annotation { "Feature Type Name" : "Feature", "Feature Type Description" : "" }
export const myFeature = defineFeature(function(context is Context, id is Id, definition is map)
    precondition{}
    {
        {
            var Q0;
            Q0=qCreatedBy(makeId("Top.planeOp"),FACE);
            var sketch = newSketch(context, id + "F0", { "sketchPlane" : qUnion([Q0])});
            skLineSegment(sketch, "E0", {"start": v(0, -673.1) * mm, "end": v(0, 901.7) * mm});
            skLineSegment(sketch, "E1", {"start": v(0, 901.7) * mm, "end": v(438.15, 901.7) * mm});
            skLineSegment(sketch, "E2", {"start": v(438.15, 901.7) * mm, "end": v(438.15, 0) * mm});
            skLineSegment(sketch, "E3", {"start": v(438.15, 0) * mm, "end": v(1454.15, 0) * mm});
            skLineSegment(sketch, "E4.0", {"start": v(552.45, 114.3) * mm, "end": v(1454.15, 114.3) * mm});
            skLineSegment(sketch, "E4.1", {"start": v(552.45, 1016) * mm, "end": v(552.45, 114.3) * mm});
            skLineSegment(sketch, "E4.2", {"start": v(-114.3, 1016) * mm, "end": v(552.45, 1016) * mm});
            skLineSegment(sketch, "E4.3", {"start": v(-114.3, -673.1) * mm, "end": v(-114.3, 1016) * mm});
            skLineSegment(sketch, "E5.0", {"start": v(425.45, -12.7) * mm, "end": v(1454.15, -12.7) * mm});
            skLineSegment(sketch, "E5.1", {"start": v(425.45, 889) * mm, "end": v(425.45, -12.7) * mm});
            skLineSegment(sketch, "E5.2", {"start": v(12.7, 889) * mm, "end": v(425.45, 889) * mm});
            skLineSegment(sketch, "E5.3", {"start": v(12.7, -673.1) * mm, "end": v(12.7, 889) * mm});
            skFitSpline(sketch, "E6", {"points": [v(-114.3, -673.1) * mm, v(0, -673.1) * mm, v(12.7, -673.1) * mm], "startDerivative": vector(215.33, 101.54) * mm, "endDerivative": vector(15.02, 74.43) * mm});
            skFitSpline(sketch, "E7", {"points": [v(1454.15, 114.3) * mm, v(1454.15, 0) * mm, v(1454.15, -12.7) * mm], "startDerivative": vector(-157.16, -195.04) * mm, "endDerivative": vector(-135.93, -152.4) * mm});
            skLineSegment(sketch, "E8.bottom", {"start": v(30.7, -669.3) * mm, "end": v(1447.96, -669.3) * mm, "construction": true});
            skLineSegment(sketch, "E8.top", {"start": v(30.7, -660.4) * mm, "end": v(1447.96, -660.4) * mm, "construction": true});
            skLineSegment(sketch, "E8.left", {"start": v(30.7, -669.3) * mm, "end": v(30.7, -660.4) * mm, "construction": true});
            skLineSegment(sketch, "E8.right", {"start": v(1447.96, -669.3) * mm, "end": v(1447.96, -660.4) * mm, "construction": true});
            skLineSegment(sketch, "E9", {"start": v(27.37, -457.2) * mm, "end": v(1426.84, -457.2) * mm, "construction": true});
            skText(sketch, "E10", { "text": "Clothes\n", "fontName": "OpenSans-Regular.ttf"});
            skText(sketch, "E11", { "text": "Hanger Rod", "fontName": "OpenSans-Regular.ttf"});
            skLineSegment(sketch, "E12", {"start": v(-114.3, 584.2) * mm, "end": v(0, 584.2) * mm, "construction": true});
            skLineSegment(sketch, "E13", {"start": v(-114.3, 177.8) * mm, "end": v(0, 177.8) * mm, "construction": true});
            skLineSegment(sketch, "E14", {"start": v(438.15, 556.05) * mm, "end": v(552.45, 556.05) * mm, "construction": true});
            skLineSegment(sketch, "E15", {"start": v(958.85, 0) * mm, "end": v(958.85, 114.3) * mm, "construction": true});
            const initialGuessF0  = {"E10": [1.1723, -0.49137, 1, 0, 0.01667], "E11": [1.16785, -0.64477, 1, 0, 0.02]};
            skSetInitialGuess(sketch, initialGuessF0);
            skSolve(sketch);
        }
        {
            var Q0;
            {var subQ2=sQuery(id+"F0.wireOp",EDGE,"E0");Q0=makeQuery(id+"F0.imprint","IMPRINT",FACE,{"disambiguationData":[TD([[makeQuery(id+"F0.imprint","IMPRINT",EDGE,{"derivedFrom":subQ2}),-1.0]])]});}
            var Q1;
            Q1=sQuery(id+"F0.wireOp",EDGE,"E0");
            var Q2;
            Q2=sQuery(id+"F0.wireOp",EDGE,"E1");
            var Q3;
            Q3=sQuery(id+"F0.wireOp",EDGE,"E2");
            var Q4;
            Q4=sQuery(id+"F0.wireOp",EDGE,"E5.1");
            var Q5;
            Q5=sQuery(id+"F0.wireOp",EDGE,"E5.2");
            var Q6;
            Q6=sQuery(id+"F0.wireOp",EDGE,"E5.3");
            var Q7;
            Q7=sQuery(id+"F0.wireOp",EDGE,"E3");
            var Q8;
            Q8=sQuery(id+"F0.wireOp",EDGE,"E5.0");
            extrude(context, id + "F1", {"entities" : qUnion([Q0]), "surfaceEntities" : qUnion([Q1, Q2, Q3, Q4, Q5, Q6, Q7, Q8]), "depth" : 127 * mm, "offsetDistance" : 25.4 * mm});
        }
        {
            var Q0;
            Q0=qCreatedBy(makeId("Front.planeOp"),FACE);
            var sketch = newSketch(context, id + "F2", { "sketchPlane" : qUnion([Q0])});
            skLineSegment(sketch, "E16.bottom", {"start": v(0, 0) * mm, "end": v(12.7, 0) * mm, "construction": true});
            skLineSegment(sketch, "E16.top", {"start": v(0, 127) * mm, "end": v(12.7, 127) * mm, "construction": true});
            skLineSegment(sketch, "E16.left", {"start": v(0, 0) * mm, "end": v(0, 127) * mm, "construction": true});
            skLineSegment(sketch, "E16.right", {"start": v(12.7, 0) * mm, "end": v(12.7, 127) * mm, "construction": true});
            skLineSegment(sketch, "E17.bottom", {"start": v(438.15, 0) * mm, "end": v(425.45, 0) * mm, "construction": true});
            skLineSegment(sketch, "E17.top", {"start": v(438.15, 127) * mm, "end": v(425.45, 127) * mm, "construction": true});
            skLineSegment(sketch, "E17.left", {"start": v(438.15, 0) * mm, "end": v(438.15, 127) * mm, "construction": true});
            skLineSegment(sketch, "E17.right", {"start": v(425.45, 0) * mm, "end": v(425.45, 127) * mm, "construction": true});
            skLineSegment(sketch, "E18.bottom", {"start": v(0, 0) * mm, "end": v(438.15, 0) * mm, "construction": true});
            skLineSegment(sketch, "E18.top", {"start": v(0, 2438.4) * mm, "end": v(438.15, 2438.4) * mm, "construction": true});
            skLineSegment(sketch, "E18.left", {"start": v(0, 0) * mm, "end": v(0, 2438.4) * mm, "construction": true});
            skLineSegment(sketch, "E18.right", {"start": v(438.15, 0) * mm, "end": v(438.15, 2438.4) * mm, "construction": true});
            skLineSegment(sketch, "E19", {"start": v(958.85, 0) * mm, "end": v(958.85, 2438.4) * mm, "construction": true});
            skLineSegment(sketch, "E20", {"start": v(565.15, 0) * mm, "end": v(565.15, 2438.4) * mm, "construction": true});
            skSolve(sketch);
        }
        {
            var Q0;
            Q0=qCreatedBy(makeId("Front.planeOp"),FACE);
            cPlane(context, id + "F3", {"entities" : qUnion([Q0]), "cplaneType" : CPlaneType.OFFSET, "offset" : 17.45 * mm, "width" : 152.4 * mm, "height" : 152.4 * mm});
        }
        {
            var Q0;
            Q0=qCreatedBy(id+"F3.planeOp",FACE);
            var sketch = newSketch(context, id + "F4", { "sketchPlane" : qUnion([Q0])});
            skLineSegment(sketch, "E21.bottom", {"start": v(55.58, 139.7) * mm, "end": v(569.93, 139.7) * mm});
            skLineSegment(sketch, "E21.top", {"start": v(55.58, 1676.4) * mm, "end": v(569.93, 1676.4) * mm});
            skLineSegment(sketch, "E21.left", {"start": v(55.58, 139.7) * mm, "end": v(55.58, 1676.4) * mm});
            skLineSegment(sketch, "E21.right", {"start": v(569.93, 139.7) * mm, "end": v(569.93, 1676.4) * mm});
            skLineSegment(sketch, "E22", {"start": v(55.58, 1295.4) * mm, "end": v(569.93, 1295.4) * mm});
            skLineSegment(sketch, "E23", {"start": v(55.58, 914.4) * mm, "end": v(569.93, 914.4) * mm});
            skLineSegment(sketch, "E24", {"start": v(55.58, 533.4) * mm, "end": v(569.93, 533.4) * mm});
            skLineSegment(sketch, "E25", {"start": v(55.58, 152.4) * mm, "end": v(569.93, 152.4) * mm, "construction": true});
            skCircle(sketch, "E26", {"center": v(109.55, 1631.95) * mm, "radius": 4.33 * mm});
            skCircle(sketch, "E27", {"center": v(109.55, 1339.85) * mm, "radius": 4.33 * mm});
            skCircle(sketch, "E28", {"center": v(109.55, 1250.95) * mm, "radius": 4.33 * mm});
            skCircle(sketch, "E29", {"center": v(109.55, 958.85) * mm, "radius": 4.33 * mm});
            skCircle(sketch, "E30", {"center": v(109.55, 869.95) * mm, "radius": 4.33 * mm});
            skCircle(sketch, "E31", {"center": v(109.55, 577.85) * mm, "radius": 4.33 * mm});
            skCircle(sketch, "E32", {"center": v(109.55, 488.95) * mm, "radius": 4.33 * mm});
            skCircle(sketch, "E33", {"center": v(109.55, 196.85) * mm, "radius": 4.33 * mm});
            skLineSegment(sketch, "E34", {"start": v(109.55, 1631.95) * mm, "end": v(109.55, 196.85) * mm, "construction": true});
            skCircle(sketch, "E35", {"center": v(515.95, 1631.95) * mm, "radius": 4.33 * mm});
            skCircle(sketch, "E36", {"center": v(515.95, 1339.85) * mm, "radius": 4.33 * mm});
            skCircle(sketch, "E37", {"center": v(515.95, 1250.95) * mm, "radius": 4.33 * mm});
            skCircle(sketch, "E38", {"center": v(515.95, 958.85) * mm, "radius": 4.33 * mm});
            skCircle(sketch, "E39", {"center": v(515.95, 869.95) * mm, "radius": 4.33 * mm});
            skCircle(sketch, "E40", {"center": v(515.95, 577.85) * mm, "radius": 4.33 * mm});
            skCircle(sketch, "E41", {"center": v(515.95, 488.95) * mm, "radius": 4.33 * mm});
            skCircle(sketch, "E42", {"center": v(515.95, 196.85) * mm, "radius": 4.33 * mm});
            skLineSegment(sketch, "E43", {"start": v(515.95, 1631.95) * mm, "end": v(515.95, 196.85) * mm, "construction": true});
            skLineSegment(sketch, "E44", {"start": v(109.55, 1631.95) * mm, "end": v(515.95, 1631.95) * mm, "construction": true});
            skLineSegment(sketch, "E45", {"start": v(109.55, 196.85) * mm, "end": v(515.95, 196.85) * mm, "construction": true});
            skLineSegment(sketch, "E46", {"start": v(109.55, 488.95) * mm, "end": v(515.95, 488.95) * mm, "construction": true});
            skLineSegment(sketch, "E47", {"start": v(109.55, 577.85) * mm, "end": v(515.95, 577.85) * mm, "construction": true});
            skLineSegment(sketch, "E48", {"start": v(109.55, 869.95) * mm, "end": v(515.95, 869.95) * mm, "construction": true});
            skLineSegment(sketch, "E49", {"start": v(109.55, 958.85) * mm, "end": v(515.95, 958.85) * mm, "construction": true});
            skLineSegment(sketch, "E50", {"start": v(109.55, 1250.95) * mm, "end": v(515.95, 1250.95) * mm, "construction": true});
            skLineSegment(sketch, "E51", {"start": v(109.55, 1339.85) * mm, "end": v(515.95, 1339.85) * mm, "construction": true});
            skSolve(sketch);
        }
        {
            var Q0;
            Q0=qCreatedBy(makeId("Front.planeOp"),FACE);
            var Q1;
            Q1=qBodyType(qCreatedBy(id+"F14",EDGE),BodyType.WIRE);
            cPlane(context, id + "F5", {"entities" : qUnion([Q0, Q1]), "cplaneType" : CPlaneType.OFFSET, "offset" : 12.7 * mm, "width" : 152.4 * mm, "height" : 152.4 * mm});
        }
        {
            var Q0;
            Q0=qCreatedBy(id+"F5.planeOp",FACE);
            var sketch = newSketch(context, id + "F6", { "sketchPlane" : qUnion([Q0])});
            skLineSegment(sketch, "E52", {"start": v(3.17, 177.8) * mm, "end": v(3.18, 130.18) * mm});
            skLineSegment(sketch, "E53", {"start": v(3.18, 130.18) * mm, "end": v(15.87, 130.18) * mm});
            skLineSegment(sketch, "E54", {"start": v(15.87, 130.18) * mm, "end": v(15.88, 0) * mm});
            skLineSegment(sketch, "E55", {"start": v(15.87, 0) * mm, "end": v(1219.2, 0) * mm});
            skLineSegment(sketch, "E56", {"start": v(1219.2, 0) * mm, "end": v(1219.2, 2438.4) * mm});
            skLineSegment(sketch, "E57", {"start": v(1219.2, 2438.4) * mm, "end": v(0, 2438.4) * mm});
            skLineSegment(sketch, "E58", {"start": v(0, 2438.4) * mm, "end": v(0, 1651) * mm});
            skLineSegment(sketch, "E59", {"start": v(0, 1651) * mm, "end": v(544.53, 1651) * mm});
            skLineSegment(sketch, "E60", {"start": v(544.53, 1651) * mm, "end": v(544.53, 177.8) * mm});
            skLineSegment(sketch, "E61", {"start": v(544.53, 177.8) * mm, "end": v(3.17, 177.8) * mm});
            skSolve(sketch);
        }
        {
            var Q0;
            Q0=makeQuery(id+"F6.imprint","IMPRINT",FACE,{"disambiguationData":[TD([[makeQuery(id+"F6.imprint","IMPRINT",EDGE,{"derivedFrom":sQuery(id+"F6.wireOp",EDGE,"E52")}),1.0]])]});
            extrude(context, id + "F7", {"entities" : qUnion([Q0]), "depth" : 4.75 * mm, "offsetDistance" : 25.4 * mm});
        }
        {
            var Q0;
            Q0=qCreatedBy(id+"F5.planeOp",FACE);
            var sketch = newSketch(context, id + "F8", { "sketchPlane" : qUnion([Q0])});
            skLineSegment(sketch, "E62.bottom", {"start": v(1219.2, 2438.4) * mm, "end": v(1181.1, 2438.4) * mm});
            skLineSegment(sketch, "E62.top", {"start": v(1219.2, 133.35) * mm, "end": v(1181.1, 133.35) * mm});
            skLineSegment(sketch, "E62.left", {"start": v(1219.2, 2438.4) * mm, "end": v(1219.2, 133.35) * mm});
            skLineSegment(sketch, "E62.right", {"start": v(1181.1, 2438.4) * mm, "end": v(1181.1, 133.35) * mm});
            skLineSegment(sketch, "E63.bottom", {"start": v(38.1, 1689.1) * mm, "end": v(1181.1, 1689.1) * mm});
            skLineSegment(sketch, "E63.top", {"start": v(38.1, 1651) * mm, "end": v(1181.1, 1651) * mm});
            skLineSegment(sketch, "E63.right", {"start": v(1181.1, 1689.1) * mm, "end": v(1181.1, 1651) * mm});
            skLineSegment(sketch, "E64.bottom", {"start": v(38.1, 1936.75) * mm, "end": v(1181.1, 1936.75) * mm});
            skLineSegment(sketch, "E64.top", {"start": v(38.1, 1898.65) * mm, "end": v(1181.1, 1898.65) * mm});
            skLineSegment(sketch, "E64.left", {"start": v(38.1, 1936.75) * mm, "end": v(38.1, 1898.65) * mm});
            skLineSegment(sketch, "E64.right", {"start": v(1181.1, 1936.75) * mm, "end": v(1181.1, 1898.65) * mm});
            skLineSegment(sketch, "E65.bottom", {"start": v(38.1, 2190.75) * mm, "end": v(1181.1, 2190.75) * mm});
            skLineSegment(sketch, "E65.top", {"start": v(38.1, 2152.65) * mm, "end": v(1181.1, 2152.65) * mm});
            skLineSegment(sketch, "E65.left", {"start": v(38.1, 2190.75) * mm, "end": v(38.1, 2152.65) * mm});
            skLineSegment(sketch, "E65.right", {"start": v(1181.1, 2190.75) * mm, "end": v(1181.1, 2152.65) * mm});
            skLineSegment(sketch, "E66.bottom", {"start": v(38.1, 2438.4) * mm, "end": v(1181.1, 2438.4) * mm});
            skLineSegment(sketch, "E66.top", {"start": v(38.1, 2400.3) * mm, "end": v(1181.1, 2400.3) * mm});
            skLineSegment(sketch, "E66.left", {"start": v(38.1, 2438.4) * mm, "end": v(38.1, 2400.3) * mm});
            skLineSegment(sketch, "E66.right", {"start": v(1181.1, 2438.4) * mm, "end": v(1181.1, 2400.3) * mm});
            skLineSegment(sketch, "E67.bottom", {"start": v(582.63, 1377.95) * mm, "end": v(1181.1, 1377.95) * mm});
            skLineSegment(sketch, "E67.top", {"start": v(582.63, 1339.85) * mm, "end": v(1181.1, 1339.85) * mm});
            skLineSegment(sketch, "E67.left", {"start": v(582.63, 1377.95) * mm, "end": v(582.63, 1339.85) * mm});
            skLineSegment(sketch, "E67.right", {"start": v(1181.1, 1377.95) * mm, "end": v(1181.1, 1339.85) * mm});
            skLineSegment(sketch, "E68.bottom", {"start": v(544.53, 1651) * mm, "end": v(582.63, 1651) * mm});
            skLineSegment(sketch, "E68.top", {"start": v(544.53, 133.35) * mm, "end": v(582.63, 133.35) * mm});
            skLineSegment(sketch, "E68.left", {"start": v(544.53, 1651) * mm, "end": v(544.53, 133.35) * mm});
            skLineSegment(sketch, "E68.right", {"start": v(582.63, 1651) * mm, "end": v(582.63, 133.35) * mm});
            skLineSegment(sketch, "E69.bottom", {"start": v(582.63, 1073.15) * mm, "end": v(1181.1, 1073.15) * mm});
            skLineSegment(sketch, "E69.top", {"start": v(582.63, 1035.05) * mm, "end": v(1181.1, 1035.05) * mm});
            skLineSegment(sketch, "E69.left", {"start": v(582.63, 1073.15) * mm, "end": v(582.63, 1035.05) * mm});
            skLineSegment(sketch, "E69.right", {"start": v(1181.1, 1073.15) * mm, "end": v(1181.1, 1035.05) * mm});
            skLineSegment(sketch, "E70.bottom", {"start": v(582.63, 768.35) * mm, "end": v(1181.1, 768.35) * mm});
            skLineSegment(sketch, "E70.top", {"start": v(582.63, 730.25) * mm, "end": v(1181.1, 730.25) * mm});
            skLineSegment(sketch, "E70.left", {"start": v(582.63, 768.35) * mm, "end": v(582.63, 730.25) * mm});
            skLineSegment(sketch, "E70.right", {"start": v(1181.1, 768.35) * mm, "end": v(1181.1, 730.25) * mm});
            skLineSegment(sketch, "E71.bottom", {"start": v(582.63, 463.55) * mm, "end": v(1181.1, 463.55) * mm});
            skLineSegment(sketch, "E71.top", {"start": v(582.63, 425.45) * mm, "end": v(1181.1, 425.45) * mm});
            skLineSegment(sketch, "E71.left", {"start": v(582.63, 463.55) * mm, "end": v(582.63, 425.45) * mm});
            skLineSegment(sketch, "E71.right", {"start": v(1181.1, 463.55) * mm, "end": v(1181.1, 425.45) * mm});
            skLineSegment(sketch, "E72.bottom", {"start": v(15.88, 127) * mm, "end": v(422.28, 127) * mm});
            skLineSegment(sketch, "E72.top", {"start": v(15.88, 0) * mm, "end": v(422.28, 0) * mm});
            skLineSegment(sketch, "E72.left", {"start": v(15.87, 127) * mm, "end": v(15.87, 0) * mm});
            skLineSegment(sketch, "E72.right", {"start": v(422.28, 127) * mm, "end": v(422.28, 0) * mm});
            skLineSegment(sketch, "E73.bottom", {"start": v(3.18, 177.8) * mm, "end": v(544.53, 177.8) * mm});
            skLineSegment(sketch, "E73.top", {"start": v(3.18, 139.7) * mm, "end": v(544.53, 139.7) * mm});
            skLineSegment(sketch, "E73.left", {"start": v(3.17, 177.8) * mm, "end": v(3.18, 139.7) * mm});
            skLineSegment(sketch, "E73.right", {"start": v(544.53, 177.8) * mm, "end": v(544.53, 139.7) * mm});
            skLineSegment(sketch, "E74.bottom", {"start": v(0, 2438.4) * mm, "end": v(38.1, 2438.4) * mm});
            skLineSegment(sketch, "E74.top", {"start": v(0, 1651) * mm, "end": v(38.1, 1651) * mm});
            skLineSegment(sketch, "E74.left", {"start": v(0, 2438.4) * mm, "end": v(0, 1651) * mm});
            skLineSegment(sketch, "E74.right", {"start": v(38.1, 2438.4) * mm, "end": v(38.1, 1651) * mm});
            skLineSegment(sketch, "E75", {"start": v(38.1, 1689.1) * mm, "end": v(38.1, 1651) * mm});
            skSolve(sketch);
        }
        {
            var Q0;
            Q0=qCreatedBy(makeId("Top.planeOp"),FACE);
            cPlane(context, id + "F9", {"entities" : qUnion([Q0]), "cplaneType" : CPlaneType.OFFSET, "offset" : 1524 * mm, "width" : 152.4 * mm, "height" : 152.4 * mm});
        }
        {
            var Q0;
            Q0=qCreatedBy(id+"F9.planeOp",FACE);
            var sketch = newSketch(context, id + "F10", { "sketchPlane" : qUnion([Q0])});
            skLineSegment(sketch, "E76.bottom", {"start": v(0, -107.95) * mm, "end": v(19.05, -107.95) * mm});
            skLineSegment(sketch, "E76.top", {"start": v(0, 857.25) * mm, "end": v(19.05, 857.25) * mm});
            skLineSegment(sketch, "E76.left", {"start": v(0, -107.95) * mm, "end": v(0, 857.25) * mm});
            skLineSegment(sketch, "E76.right", {"start": v(19.05, -107.95) * mm, "end": v(19.05, 857.25) * mm});
            skLineSegment(sketch, "E77.bottom", {"start": v(19.05, 87.31) * mm, "end": v(21.59, 87.31) * mm});
            skLineSegment(sketch, "E77.top", {"start": v(19.05, -158.75) * mm, "end": v(21.6, -158.75) * mm});
            skLineSegment(sketch, "E77.left", {"start": v(19.05, 87.31) * mm, "end": v(19.05, -158.75) * mm});
            skLineSegment(sketch, "E77.right", {"start": v(21.59, 87.31) * mm, "end": v(21.6, -158.75) * mm});
            skLineSegment(sketch, "E78", {"start": v(19.05, -158.75) * mm, "end": v(26.99, -158.75) * mm, "construction": true});
            skCircle(sketch, "E79", {"center": v(26.99, -158.75) * mm, "radius": 2.8 * mm});
            skCircle(sketch, "E80", {"center": v(26.99, -158.75) * mm, "radius": 7.94 * mm});
            skLineSegment(sketch, "E81.bottom", {"start": v(0, -254) * mm, "end": v(12.7, -254) * mm});
            skLineSegment(sketch, "E81.top", {"start": v(0, -171.45) * mm, "end": v(12.7, -171.45) * mm});
            skLineSegment(sketch, "E81.left", {"start": v(0, -171.45) * mm, "end": v(0, -254) * mm});
            skLineSegment(sketch, "E81.right", {"start": v(12.7, -171.45) * mm, "end": v(12.7, -254) * mm});
            skCircle(sketch, "E82", {"center": v(26.99, -158.75) * mm, "radius": 24.8 * mm, "construction": true});
            skLineSegment(sketch, "E83", {"start": v(-131.72, -179.39) * mm, "end": v(182.58, -179.39) * mm, "construction": true});
            skSolve(sketch);
        }
        {
            var Q0;
            Q0=qCreatedBy(makeId("Top.planeOp"),FACE);
            cPlane(context, id + "F11", {"entities" : qUnion([Q0]), "cplaneType" : CPlaneType.OFFSET, "offset" : 1668.48 * mm, "width" : 152.4 * mm, "height" : 152.4 * mm});
        }
        {
            var Q0;
            Q0=qCreatedBy(id+"F11.planeOp",FACE);
            var sketch = newSketch(context, id + "F12", { "sketchPlane" : qUnion([Q0])});
            skLineSegment(sketch, "E84.bottom", {"start": v(55.58, -17.45) * mm, "end": v(569.93, -17.45) * mm});
            skLineSegment(sketch, "E84.top", {"start": v(55.58, -179.37) * mm, "end": v(569.93, -179.37) * mm});
            skLineSegment(sketch, "E84.left", {"start": v(55.58, -17.45) * mm, "end": v(55.58, -179.37) * mm});
            skLineSegment(sketch, "E84.right", {"start": v(569.93, -17.45) * mm, "end": v(569.93, -179.37) * mm});
            skLineSegment(sketch, "E85.bottom", {"start": v(34.93, -158.75) * mm, "end": v(32.39, -158.75) * mm});
            skLineSegment(sketch, "E85.top", {"start": v(34.92, 86.78) * mm, "end": v(32.39, 86.78) * mm});
            skLineSegment(sketch, "E85.left", {"start": v(34.93, -158.75) * mm, "end": v(34.93, 86.78) * mm});
            skLineSegment(sketch, "E85.right", {"start": v(32.39, -158.75) * mm, "end": v(32.39, 86.78) * mm});
            skLineSegment(sketch, "E86", {"start": v(34.93, -158.75) * mm, "end": v(26.99, -158.75) * mm, "construction": true});
            skArc(sketch, "E87", {"start": v(569.93, -17.45) * mm, "mid": v(470.85, -501.88) * mm, "end": v(26.99, -719.77) * mm, "construction": true});
            skLineSegment(sketch, "E88.bottom", {"start": v(7.14, -171.45) * mm, "end": v(55.58, -171.45) * mm});
            skLineSegment(sketch, "E88.top", {"start": v(4.78, -120.65) * mm, "end": v(55.58, -120.65) * mm});
            skLineSegment(sketch, "E88.left", {"start": v(4.78, -169.09) * mm, "end": v(4.78, -120.65) * mm});
            skLineSegment(sketch, "E88.right", {"start": v(55.58, -171.45) * mm, "end": v(55.58, -120.65) * mm});
            skLineSegment(sketch, "E89", {"start": v(38.92, -168.27) * mm, "end": v(-16.3, -168.27) * mm, "construction": true});
            skLineSegment(sketch, "E90.bottom", {"start": v(34.92, 0) * mm, "end": v(415.93, 0) * mm});
            skLineSegment(sketch, "E90.top", {"start": v(34.92, 19.05) * mm, "end": v(415.93, 19.05) * mm});
            skLineSegment(sketch, "E90.left", {"start": v(34.93, 0) * mm, "end": v(34.93, 19.05) * mm});
            skLineSegment(sketch, "E90.right", {"start": v(415.93, 0) * mm, "end": v(415.93, 19.05) * mm});
            skPoint(sketch, "E91.visualSharp", {"position": v(4.78, -171.45) * mm});
            skArc(sketch, "E91.filletArc", {"start": v(4.78, -169.09) * mm, "mid": v(5.47, -170.76) * mm, "end": v(7.14, -171.45) * mm});
            skCircle(sketch, "E92", {"center": v(26.99, -158.75) * mm, "radius": 44.1 * mm, "construction": true});
            skLineSegment(sketch, "E93.bottom", {"start": v(29.84, -130.8) * mm, "end": v(32.38, -130.8) * mm});
            skLineSegment(sketch, "E93.left", {"start": v(29.84, -130.8) * mm, "end": v(29.84, 21.6) * mm});
            skLineSegment(sketch, "E94.bottom", {"start": v(29.84, 21.6) * mm, "end": v(182.25, 21.6) * mm});
            skLineSegment(sketch, "E94.right", {"start": v(182.25, 21.6) * mm, "end": v(182.25, 19.05) * mm});
            skLineSegment(sketch, "E95.0", {"start": v(32.38, 19.05) * mm, "end": v(182.25, 19.05) * mm});
            skLineSegment(sketch, "E95.1", {"start": v(32.38, -130.8) * mm, "end": v(32.38, 19.05) * mm});
            skLineSegment(sketch, "E96", {"start": v(29.01, -139.7) * mm, "end": v(52.14, -139.7) * mm, "construction": true});
            skSolve(sketch);
        }
        {
            var Q0;
            Q0=qSketchRegion(id+"F4",true);
            extrude(context, id + "F13", {"entities" : qUnion([Q0]), "depth" : 161.92 * mm, "offsetDistance" : 25.4 * mm});
        }
        {
            var Q0;
            Q0=qCreatedBy(id+"F3.planeOp",FACE);
            var sketch = newSketch(context, id + "F14", { "sketchPlane" : qUnion([Q0])});
            skLineSegment(sketch, "E97.0", {"start": v(538.18, 184.15) * mm, "end": v(61.93, 184.15) * mm});
            skLineSegment(sketch, "E97.1", {"start": v(538.18, 1644.65) * mm, "end": v(538.18, 184.15) * mm});
            skLineSegment(sketch, "E97.2", {"start": v(61.93, 1644.65) * mm, "end": v(538.18, 1644.65) * mm});
            skLineSegment(sketch, "E98", {"start": v(61.93, 1644.65) * mm, "end": v(61.93, 184.15) * mm});
            skSolve(sketch);
        }
        {
            var Q0;
            Q0=qCreatedBy(id+"F3.planeOp",FACE);
            cPlane(context, id + "F15", {"entities" : qUnion([Q0]), "cplaneType" : CPlaneType.OFFSET, "offset" : 17.45 * mm, "oppositeDirection" : true, "width" : 152.4 * mm, "height" : 152.4 * mm});
        }
        {
            var Q0;
            Q0=qCreatedBy(id+"F15.planeOp",FACE);
            var sketch = newSketch(context, id + "F16", { "sketchPlane" : qUnion([Q0])});
            skLineSegment(sketch, "E99.bottom", {"start": v(34.92, 1644.65) * mm, "end": v(415.93, 1644.65) * mm});
            skLineSegment(sketch, "E99.top", {"start": v(34.93, 184.15) * mm, "end": v(415.93, 184.15) * mm});
            skLineSegment(sketch, "E99.left", {"start": v(34.92, 1644.65) * mm, "end": v(34.93, 184.15) * mm});
            skLineSegment(sketch, "E99.right", {"start": v(415.93, 1644.65) * mm, "end": v(415.93, 184.15) * mm});
            skLineSegment(sketch, "E100", {"start": v(34.93, 533.4) * mm, "end": v(415.93, 533.4) * mm, "construction": true});
            skLineSegment(sketch, "E101", {"start": v(34.93, 1295.4) * mm, "end": v(415.93, 1295.4) * mm, "construction": true});
            skSolve(sketch);
        }
        {
            var Q0;
            Q0=qCreatedBy(id+"F15.planeOp",FACE);
            var sketch = newSketch(context, id + "F17", { "sketchPlane" : qUnion([Q0])});
            skLineSegment(sketch, "E102.bottom", {"start": v(55.58, 1644.65) * mm, "end": v(538.18, 1644.65) * mm});
            skLineSegment(sketch, "E102.top", {"start": v(55.58, 1593.85) * mm, "end": v(538.18, 1593.85) * mm});
            skLineSegment(sketch, "E102.left", {"start": v(55.58, 1644.65) * mm, "end": v(55.58, 1593.85) * mm});
            skLineSegment(sketch, "E102.right", {"start": v(538.18, 1644.65) * mm, "end": v(538.18, 1593.85) * mm});
            skLineSegment(sketch, "E103.bottom", {"start": v(34.93, 603.25) * mm, "end": v(538.18, 603.25) * mm});
            skLineSegment(sketch, "E103.top", {"start": v(34.93, 463.55) * mm, "end": v(538.18, 463.55) * mm});
            skLineSegment(sketch, "E103.left", {"start": v(34.93, 603.25) * mm, "end": v(34.93, 463.55) * mm});
            skLineSegment(sketch, "E103.right", {"start": v(538.18, 603.25) * mm, "end": v(538.18, 463.55) * mm});
            skLineSegment(sketch, "E104.bottom", {"start": v(55.58, 234.95) * mm, "end": v(538.18, 234.95) * mm});
            skLineSegment(sketch, "E104.top", {"start": v(55.58, 184.15) * mm, "end": v(538.18, 184.15) * mm});
            skLineSegment(sketch, "E104.left", {"start": v(55.58, 234.95) * mm, "end": v(55.58, 184.15) * mm});
            skLineSegment(sketch, "E104.right", {"start": v(538.18, 234.95) * mm, "end": v(538.18, 184.15) * mm});
            skLineSegment(sketch, "E105.bottom", {"start": v(34.93, 1365.25) * mm, "end": v(538.18, 1365.25) * mm});
            skLineSegment(sketch, "E105.top", {"start": v(34.93, 1225.55) * mm, "end": v(538.18, 1225.55) * mm});
            skLineSegment(sketch, "E105.left", {"start": v(34.93, 1365.25) * mm, "end": v(34.93, 1225.55) * mm});
            skLineSegment(sketch, "E105.right", {"start": v(538.18, 1365.25) * mm, "end": v(538.18, 1225.55) * mm});
            skLineSegment(sketch, "E106.bottom", {"start": v(34.93, 984.25) * mm, "end": v(538.18, 984.25) * mm});
            skLineSegment(sketch, "E106.top", {"start": v(34.93, 844.55) * mm, "end": v(538.18, 844.55) * mm});
            skLineSegment(sketch, "E106.left", {"start": v(34.93, 984.25) * mm, "end": v(34.93, 844.55) * mm});
            skLineSegment(sketch, "E106.right", {"start": v(538.18, 984.25) * mm, "end": v(538.18, 844.55) * mm});
            skLineSegment(sketch, "E107.bottom", {"start": v(55.58, 1668.48) * mm, "end": v(4.78, 1668.48) * mm});
            skLineSegment(sketch, "E107.top", {"start": v(55.58, 1617.68) * mm, "end": v(4.78, 1617.68) * mm});
            skLineSegment(sketch, "E107.left", {"start": v(55.58, 1668.48) * mm, "end": v(55.58, 1617.68) * mm});
            skLineSegment(sketch, "E107.right", {"start": v(4.78, 1668.48) * mm, "end": v(4.78, 1617.68) * mm});
            skLineSegment(sketch, "E108.bottom", {"start": v(55.58, 211.12) * mm, "end": v(4.78, 211.12) * mm});
            skLineSegment(sketch, "E108.top", {"start": v(55.58, 160.32) * mm, "end": v(4.78, 160.32) * mm});
            skLineSegment(sketch, "E108.left", {"start": v(55.58, 211.12) * mm, "end": v(55.58, 160.32) * mm});
            skLineSegment(sketch, "E108.right", {"start": v(4.78, 211.12) * mm, "end": v(4.78, 160.32) * mm});
            skSolve(sketch);
        }
        {
            var Q0;
            Q0=qSketchRegion(id+"F16",true);
            extrude(context, id + "F18", {"entities" : qUnion([Q0]), "oppositeDirection" : true, "depth" : 19.05 * mm, "offsetDistance" : 25.4 * mm});
        }
        {
            var Q0;
            {var subQ9=sQuery(id+"F12.wireOp",EDGE,"E85.bottom");Q0=makeQuery(id+"F12.imprint","IMPRINT",FACE,{"disambiguationData":[TD([[makeQuery(id+"F12.imprint","IMPRINT",EDGE,{"derivedFrom":subQ9}),1.0]])]});}
            var Q1;
            {var subQ1=sQuery(id+"F12.wireOp",EDGE,"E85.bottom");Q1=makeQuery(id+"F12.imprint","IMPRINT",FACE,{"disambiguationData":[TD([[makeQuery(id+"F12.imprint","IMPRINT",EDGE,{"derivedFrom":subQ1}),-1.0]])]});}
            var Q2;
            {var subQ3=sQuery(id+"F12.wireOp",EDGE,"E93.bottom");Q2=makeQuery(id+"F12.imprint","IMPRINT",FACE,{"disambiguationData":[TD([[makeQuery(id+"F12.imprint","IMPRINT",EDGE,{"derivedFrom":subQ3}),1.0]])]});}
            var Q3;
            Q3=sQuery(id+"F12.wireOp",EDGE,"E88.top");
            var Q4;
            Q4=sQuery(id+"F12.wireOp",EDGE,"E88.right");
            var Q5;
            Q5=sQuery(id+"F12.wireOp",EDGE,"E88.bottom");
            var Q6;
            Q6=sQuery(id+"F12.wireOp",EDGE,"E88.left");
            extrude(context, id + "F19", {"entities" : qUnion([Q0, Q1, Q2]), "surfaceEntities" : qUnion([Q3, Q4, Q5, Q6]), "oppositeDirection" : true, "depth" : 1508.12 * mm, "offsetDistance" : 25.4 * mm});
        }
        {
            var Q0;
            {var subQ3=sQuery(id+"F17.wireOp",EDGE,"E107.bottom");Q0=makeQuery(id+"F17.imprint","IMPRINT",FACE,{"disambiguationData":[TD([[makeQuery(id+"F17.imprint","IMPRINT",EDGE,{"derivedFrom":subQ3}),1.0]])]});}
            var Q1;
            {var subQ3=sQuery(id+"F17.wireOp",EDGE,"E108.bottom");Q1=makeQuery(id+"F17.imprint","IMPRINT",FACE,{"disambiguationData":[TD([[makeQuery(id+"F17.imprint","IMPRINT",EDGE,{"derivedFrom":subQ3}),1.0]])]});}
            var Q2;
            Q2=sQuery(id+"F17.wireOp",EDGE,"E108.bottom");
            var Q3;
            Q3=sQuery(id+"F17.wireOp",EDGE,"E108.right");
            var Q4;
            Q4=sQuery(id+"F17.wireOp",EDGE,"E108.top");
            var Q5;
            Q5=sQuery(id+"F17.wireOp",EDGE,"E108.left");
            var Q6;
            Q6=sQuery(id+"F17.wireOp",EDGE,"E107.right");
            var Q7;
            Q7=sQuery(id+"F17.wireOp",EDGE,"E107.bottom");
            var Q8;
            Q8=sQuery(id+"F17.wireOp",EDGE,"E107.left");
            var Q9;
            Q9=sQuery(id+"F17.wireOp",EDGE,"E107.top");
            var Q10;
            Q10=makeQuery(id+"F19.opExtrude","SWEPT_FACE",FACE,{"disambiguationData":[OSD([sQuery(id+"F12.wireOp",EDGE,"E88.top")])]});
            extrude(context, id + "F20", {"entities" : qUnion([Q0, Q1]), "surfaceEntities" : qUnion([Q2, Q3, Q4, Q5, Q6, Q7, Q8, Q9]), "endBound" : BoundingType.UP_TO_SURFACE, "depth" : 25.4 * mm, "endBoundEntityFace" : qUnion([Q10]), "offsetDistance" : 25.4 * mm});
        }
        {
            var Q0;
            {var subQ2=sQuery(id+"F17.wireOp",EDGE,"E102.bottom");Q0=makeQuery(id+"F17.imprint","IMPRINT",FACE,{"disambiguationData":[TD([[makeQuery(id+"F17.imprint","IMPRINT",EDGE,{"derivedFrom":subQ2}),-1.0]])]});}
            var Q1;
            Q1=makeQuery(id+"F17.imprint","IMPRINT",FACE,{"disambiguationData":[TD([[makeQuery(id+"F17.imprint","IMPRINT",EDGE,{"derivedFrom":sQuery(id+"F17.wireOp",EDGE,"E105.bottom")}),-1.0]])]});
            var Q2;
            Q2=makeQuery(id+"F17.imprint","IMPRINT",FACE,{"disambiguationData":[TD([[makeQuery(id+"F17.imprint","IMPRINT",EDGE,{"derivedFrom":sQuery(id+"F17.wireOp",EDGE,"E106.bottom")}),-1.0]])]});
            var Q3;
            Q3=makeQuery(id+"F17.imprint","IMPRINT",FACE,{"disambiguationData":[TD([[makeQuery(id+"F17.imprint","IMPRINT",EDGE,{"derivedFrom":sQuery(id+"F17.wireOp",EDGE,"E103.bottom")}),-1.0]])]});
            var Q4;
            Q4=makeQuery(id+"F17.imprint","IMPRINT",FACE,{"disambiguationData":[TD([[makeQuery(id+"F17.imprint","IMPRINT",EDGE,{"derivedFrom":sQuery(id+"F17.wireOp",EDGE,"E104.bottom")}),-1.0]])]});
            extrude(context, id + "F21", {"entities" : qUnion([Q0, Q1, Q2, Q3, Q4]), "depth" : 12.7 * mm, "offsetDistance" : 25.4 * mm});
        }
        {
            var Q0;
            Q0=qCreatedBy(makeId("Right.planeOp"),FACE);
            var sketch = newSketch(context, id + "F22", { "sketchPlane" : qUnion([Q0])});
            skLineSegment(sketch, "E109", {"start": v(0, 2438.4) * mm, "end": v(903.42, 2438.4) * mm, "construction": true});
            skLineSegment(sketch, "E110", {"start": v(903.42, 0) * mm, "end": v(903.42, 2438.4) * mm, "construction": true});
            skLineSegment(sketch, "E111.bottom", {"start": v(-107.95, 1614.5) * mm, "end": v(857.25, 1614.5) * mm});
            skLineSegment(sketch, "E111.top", {"start": v(-107.95, 214.3) * mm, "end": v(857.25, 214.3) * mm});
            skLineSegment(sketch, "E111.left", {"start": v(-107.95, 1614.5) * mm, "end": v(-107.95, 214.3) * mm});
            skLineSegment(sketch, "E111.right", {"start": v(857.25, 1614.5) * mm, "end": v(857.25, 214.3) * mm});
            skLineSegment(sketch, "E112", {"start": v(903.42, 1295.4) * mm, "end": v(-285.88, 1295.4) * mm, "construction": true});
            skLineSegment(sketch, "E113", {"start": v(903.42, 533.4) * mm, "end": v(-311.78, 533.4) * mm, "construction": true});
            skLineSegment(sketch, "E114.bottom", {"start": v(-254, 1760.55) * mm, "end": v(-171.45, 1760.55) * mm});
            skLineSegment(sketch, "E114.top", {"start": v(-254, 127) * mm, "end": v(-171.45, 127) * mm});
            skLineSegment(sketch, "E114.left", {"start": v(-254, 1760.55) * mm, "end": v(-254, 127) * mm});
            skLineSegment(sketch, "E114.right", {"start": v(-171.45, 1760.55) * mm, "end": v(-171.45, 127) * mm});
            skLineSegment(sketch, "E115.bottom", {"start": v(-171.45, 1754.2) * mm, "end": v(-17.45, 1754.2) * mm});
            skLineSegment(sketch, "E115.top", {"start": v(-171.45, 1671.65) * mm, "end": v(-17.45, 1671.65) * mm});
            skLineSegment(sketch, "E115.left", {"start": v(-171.45, 1754.2) * mm, "end": v(-171.45, 1671.65) * mm});
            skLineSegment(sketch, "E115.right", {"start": v(-17.45, 1754.2) * mm, "end": v(-17.45, 1671.65) * mm});
            skLineSegment(sketch, "E116", {"start": v(584.2, 2438.4) * mm, "end": v(584.2, 0) * mm, "construction": true});
            skLineSegment(sketch, "E117", {"start": v(177.8, 2438.4) * mm, "end": v(177.8, 0) * mm, "construction": true});
            skLineSegment(sketch, "E118", {"start": v(-149.22, 581.02) * mm, "end": v(-149.22, 485.77) * mm});
            skLineSegment(sketch, "E119", {"start": v(-149.23, 485.77) * mm, "end": v(87.31, 523.88) * mm});
            skLineSegment(sketch, "E120", {"start": v(87.31, 523.88) * mm, "end": v(87.31, 542.93) * mm});
            skLineSegment(sketch, "E121", {"start": v(87.31, 542.93) * mm, "end": v(-149.22, 581.03) * mm});
            skLineSegment(sketch, "E122.bottom", {"start": v(-149.22, 581.02) * mm, "end": v(-168.27, 581.02) * mm});
            skLineSegment(sketch, "E122.top", {"start": v(-149.22, 485.77) * mm, "end": v(-168.27, 485.77) * mm});
            skLineSegment(sketch, "E122.left", {"start": v(-149.22, 581.03) * mm, "end": v(-149.22, 485.77) * mm});
            skLineSegment(sketch, "E122.right", {"start": v(-168.27, 581.02) * mm, "end": v(-168.27, 485.77) * mm});
            skLineSegment(sketch, "E123", {"start": v(-158.75, 581.02) * mm, "end": v(-158.75, 485.78) * mm, "construction": true});
            skCircle(sketch, "E124", {"center": v(-38.1, 533.4) * mm, "radius": 3.96 * mm});
            skCircle(sketch, "E125", {"center": v(63.5, 533.4) * mm, "radius": 3.96 * mm});
            skLineSegment(sketch, "E126", {"start": v(-149.22, 1343.02) * mm, "end": v(-149.22, 1247.78) * mm});
            skLineSegment(sketch, "E127", {"start": v(-149.23, 1247.77) * mm, "end": v(87.31, 1285.88) * mm});
            skLineSegment(sketch, "E128", {"start": v(87.31, 1285.88) * mm, "end": v(87.31, 1304.93) * mm});
            skLineSegment(sketch, "E129", {"start": v(87.31, 1304.92) * mm, "end": v(-149.22, 1343.03) * mm});
            skLineSegment(sketch, "E130.bottom", {"start": v(-149.23, 1343.03) * mm, "end": v(-168.28, 1343.03) * mm});
            skLineSegment(sketch, "E130.top", {"start": v(-149.22, 1247.78) * mm, "end": v(-168.28, 1247.78) * mm});
            skLineSegment(sketch, "E130.left", {"start": v(-149.22, 1343.03) * mm, "end": v(-149.22, 1247.78) * mm});
            skLineSegment(sketch, "E130.right", {"start": v(-168.28, 1343.03) * mm, "end": v(-168.28, 1247.78) * mm});
            skLineSegment(sketch, "E131", {"start": v(-158.75, 1343.03) * mm, "end": v(-158.75, 1247.78) * mm, "construction": true});
            skCircle(sketch, "E132", {"center": v(-38.1, 1295.4) * mm, "radius": 3.96 * mm});
            skCircle(sketch, "E133", {"center": v(63.5, 1295.4) * mm, "radius": 3.96 * mm});
            skLineSegment(sketch, "E134", {"start": v(87.31, 1295.4) * mm, "end": v(-168.28, 1295.4) * mm, "construction": true});
            skSolve(sketch);
        }
        {
            var Q0;
            {var subQ10=sQuery(id+"F22.wireOp",EDGE,"E111.bottom");Q0=makeQuery(id+"F22.imprint","IMPRINT",FACE,{"disambiguationData":[TD([[makeQuery(id+"F22.imprint","IMPRINT",EDGE,{"derivedFrom":subQ10}),-1.0]])]});}
            var Q1;
            {var subQ0=sQuery(id+"F22.wireOp",EDGE,"E120");Q1=makeQuery(id+"F22.imprint","IMPRINT",FACE,{"disambiguationData":[TD([[makeQuery(id+"F22.imprint","IMPRINT",EDGE,{"derivedFrom":subQ0}),1.0]])]});}
            var Q2;
            {var subQ1=sQuery(id+"F22.wireOp",EDGE,"E128");Q2=makeQuery(id+"F22.imprint","IMPRINT",FACE,{"disambiguationData":[TD([[makeQuery(id+"F22.imprint","IMPRINT",EDGE,{"derivedFrom":subQ1}),1.0]])]});}
            extrude(context, id + "F23", {"entities" : qUnion([Q0, Q1, Q2]), "depth" : 19.05 * mm, "offsetDistance" : 25.4 * mm});
        }
        {
            var Q0;
            {var subQ2=sQuery(id+"F22.wireOp",EDGE,"E115.bottom");Q0=makeQuery(id+"F22.imprint","IMPRINT",FACE,{"disambiguationData":[TD([[makeQuery(id+"F22.imprint","IMPRINT",EDGE,{"derivedFrom":subQ2}),-1.0]])]});}
            var Q1;
            {var subQ3=sQuery(id+"F22.wireOp",EDGE,"E114.bottom");Q1=makeQuery(id+"F22.imprint","IMPRINT",FACE,{"disambiguationData":[TD([[makeQuery(id+"F22.imprint","IMPRINT",EDGE,{"derivedFrom":subQ3}),-1.0]])]});}
            extrude(context, id + "F24", {"entities" : qUnion([Q0, Q1]), "depth" : 15.08 * mm, "offsetDistance" : 25.4 * mm});
        }
        {
            var Q0;
            {var subQ0=sQuery(id+"F8.wireOp",EDGE,"E66.bottom");Q0=makeQuery(id+"F8.imprint","IMPRINT",FACE,{"disambiguationData":[TD([[makeQuery(id+"F8.imprint","IMPRINT",EDGE,{"derivedFrom":subQ0}),-1.0]])]});}
            var Q1;
            {var subQ3=sQuery(id+"F8.wireOp",EDGE,"E64.left");Q1=makeQuery(id+"F8.imprint","IMPRINT",FACE,{"disambiguationData":[TD([[makeQuery(id+"F8.imprint","IMPRINT",EDGE,{"derivedFrom":subQ3}),-1.0]])]});}
            var Q2;
            {var subQ0=sQuery(id+"F8.wireOp",EDGE,"E65.bottom");Q2=makeQuery(id+"F8.imprint","IMPRINT",FACE,{"disambiguationData":[TD([[makeQuery(id+"F8.imprint","IMPRINT",EDGE,{"derivedFrom":subQ0}),-1.0]])]});}
            var Q3;
            {var subQ2=sQuery(id+"F8.wireOp",EDGE,"E64.bottom");Q3=makeQuery(id+"F8.imprint","IMPRINT",FACE,{"disambiguationData":[TD([[makeQuery(id+"F8.imprint","IMPRINT",EDGE,{"derivedFrom":subQ2}),-1.0]])]});}
            var Q4;
            {var subQ7=sQuery(id+"F8.wireOp",EDGE,"E63.bottom");Q4=makeQuery(id+"F8.imprint","IMPRINT",FACE,{"disambiguationData":[TD([[makeQuery(id+"F8.imprint","IMPRINT",EDGE,{"derivedFrom":subQ7}),-1.0]])]});}
            var Q5;
            {var subQ13=sQuery(id+"F8.wireOp",EDGE,"E62.bottom");Q5=makeQuery(id+"F8.imprint","IMPRINT",FACE,{"disambiguationData":[TD([[makeQuery(id+"F8.imprint","IMPRINT",EDGE,{"derivedFrom":subQ13}),1.0]])]});}
            var Q6;
            {var subQ0=sQuery(id+"F8.wireOp",EDGE,"E67.bottom");Q6=makeQuery(id+"F8.imprint","IMPRINT",FACE,{"disambiguationData":[TD([[makeQuery(id+"F8.imprint","IMPRINT",EDGE,{"derivedFrom":subQ0}),-1.0]])]});}
            var Q7;
            {var subQ0=sQuery(id+"F8.wireOp",EDGE,"E69.bottom");Q7=makeQuery(id+"F8.imprint","IMPRINT",FACE,{"disambiguationData":[TD([[makeQuery(id+"F8.imprint","IMPRINT",EDGE,{"derivedFrom":subQ0}),-1.0]])]});}
            var Q8;
            {var subQ0=sQuery(id+"F8.wireOp",EDGE,"E73.bottom");Q8=makeQuery(id+"F8.imprint","IMPRINT",FACE,{"disambiguationData":[TD([[makeQuery(id+"F8.imprint","IMPRINT",EDGE,{"derivedFrom":subQ0}),-1.0]])]});}
            var Q9;
            {var subQ2=sQuery(id+"F8.wireOp",EDGE,"E71.bottom");Q9=makeQuery(id+"F8.imprint","IMPRINT",FACE,{"disambiguationData":[TD([[makeQuery(id+"F8.imprint","IMPRINT",EDGE,{"derivedFrom":subQ2}),-1.0]])]});}
            var Q10;
            {var subQ0=sQuery(id+"F8.wireOp",EDGE,"E70.bottom");Q10=makeQuery(id+"F8.imprint","IMPRINT",FACE,{"disambiguationData":[TD([[makeQuery(id+"F8.imprint","IMPRINT",EDGE,{"derivedFrom":subQ0}),-1.0]])]});}
            var Q11;
            {var subQ3=sQuery(id+"F8.wireOp",EDGE,"E67.left");Q11=makeQuery(id+"F8.imprint","IMPRINT",FACE,{"disambiguationData":[TD([[makeQuery(id+"F8.imprint","IMPRINT",EDGE,{"derivedFrom":subQ3}),-1.0]])]});}
            extrude(context, id + "F25", {"entities" : qUnion([Q0, Q1, Q2, Q3, Q4, Q5, Q6, Q7, Q8, Q9, Q10, Q11]), "oppositeDirection" : true, "depth" : 12.7 * mm, "offsetDistance" : 25.4 * mm});
        }
        {
            var Q0;
            Q0=makeQuery(id+"F8.imprint","IMPRINT",FACE,{"disambiguationData":[TD([[makeQuery(id+"F8.imprint","IMPRINT",EDGE,{"derivedFrom":sQuery(id+"F8.wireOp",EDGE,"E72.bottom")}),-1.0]])]});
            extrude(context, id + "F26", {"entities" : qUnion([Q0]), "operationType" : NewBodyOperationType.ADD, "oppositeDirection" : true, "depth" : 12.7 * mm, "offsetDistance" : 25.4 * mm});
        }
        {
            var Q0;
            Q0=makeQuery(id+"F14.imprint","IMPRINT",FACE,{"disambiguationData":[TD([[makeQuery(id+"F14.imprint","IMPRINT",EDGE,{"derivedFrom":sQuery(id+"F14.wireOp",EDGE,"E97.0")}),-1.0]])]});
            extrude(context, id + "F27", {"entities" : qUnion([Q0]), "oppositeDirection" : true, "depth" : 4.75 * mm, "offsetDistance" : 25.4 * mm});
        }
        {
            var Q0;
            Q0=qCreatedBy(makeId("Front.planeOp"),FACE);
            var sketch = newSketch(context, id + "F28", { "sketchPlane" : qUnion([Q0])});
            skLineSegment(sketch, "E135.bottom", {"start": v(0, 2438.4) * mm, "end": v(438.15, 2438.4) * mm});
            skLineSegment(sketch, "E135.top", {"start": v(0, 1651) * mm, "end": v(438.15, 1651) * mm});
            skLineSegment(sketch, "E135.left", {"start": v(0, 2438.4) * mm, "end": v(0, 1651) * mm});
            skLineSegment(sketch, "E135.right", {"start": v(438.15, 2438.4) * mm, "end": v(438.15, 1651) * mm});
            skLineSegment(sketch, "E136", {"start": v(3.17, 177.8) * mm, "end": v(3.18, 130.18) * mm});
            skLineSegment(sketch, "E137", {"start": v(3.18, 130.18) * mm, "end": v(15.87, 130.18) * mm});
            skLineSegment(sketch, "E138", {"start": v(15.87, 130.18) * mm, "end": v(15.88, 0) * mm});
            skLineSegment(sketch, "E139", {"start": v(15.88, 0) * mm, "end": v(425.45, 0) * mm});
            skLineSegment(sketch, "E140", {"start": v(425.45, 0) * mm, "end": v(425.45, 127) * mm});
            skLineSegment(sketch, "E141", {"start": v(425.45, 127) * mm, "end": v(438.15, 127) * mm});
            skLineSegment(sketch, "E142", {"start": v(438.15, 127) * mm, "end": v(438.15, 177.8) * mm});
            skLineSegment(sketch, "E143", {"start": v(438.15, 177.8) * mm, "end": v(3.18, 177.8) * mm});
            skSolve(sketch);
        }
        {
            var Q0;
            Q0=makeQuery(id+"F28.imprint","IMPRINT",FACE,{"disambiguationData":[TD([[makeQuery(id+"F28.imprint","IMPRINT",EDGE,{"derivedFrom":sQuery(id+"F28.wireOp",EDGE,"E135.bottom")}),-1.0]])]});
            var Q1;
            Q1=makeQuery(id+"F28.imprint","IMPRINT",FACE,{"disambiguationData":[TD([[makeQuery(id+"F28.imprint","IMPRINT",EDGE,{"derivedFrom":sQuery(id+"F28.wireOp",EDGE,"E136")}),1.0]])]});
            extrude(context, id + "F29", {"entities" : qUnion([Q0, Q1]), "oppositeDirection" : true, "depth" : 19.05 * mm, "offsetDistance" : 25.4 * mm});
        }
    });